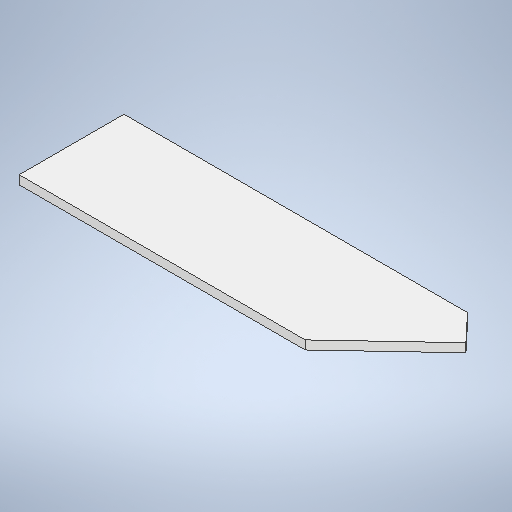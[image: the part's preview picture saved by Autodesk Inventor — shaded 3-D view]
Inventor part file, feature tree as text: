
AUTODESK INVENTOR PART (.ipt)
format: ipt  version: 2025 (Build 290162000, 162)  size: 271,872 bytes
history: native  units: in
note: dims shown in document units (in); Inventor stores cm internally (conversion verified against a paired STEP export)
features: extrude x2, sketch x2
ambient origin geometry x8: Origin, YZ Plane, XZ Plane, XY Plane, X Axis, Y Axis, Z Axis, Center Point
bodies: Solid1 (feature_tree)
feature tree (4):
  extrude  "Extrusion1"  Depth=1.5in TaperAngle=0.0deg
  extrude  "Extrusion3"  Depth=0.9157in
  sketch  "Sketch1"  dims[d6=18.0in d8=1.5in d9=0.0in]
  sketch  "Sketch3"  dims[d10=63.3483in d16=0.9157in d17=6.345in d18=1.0in d19=0.0in d20=0.5in d21=0.0344in]
